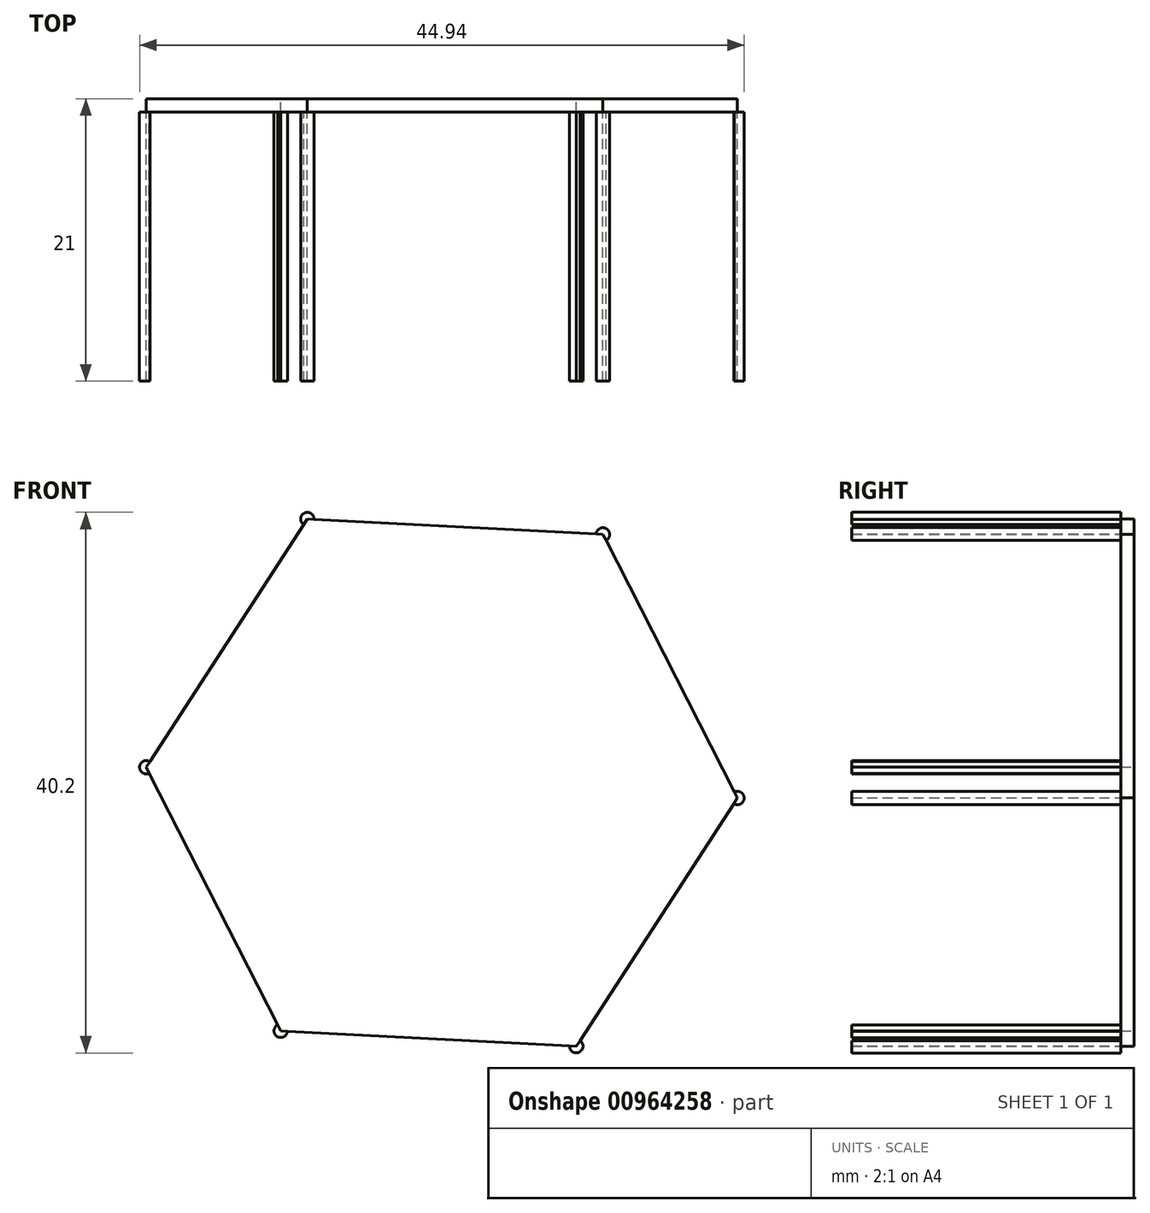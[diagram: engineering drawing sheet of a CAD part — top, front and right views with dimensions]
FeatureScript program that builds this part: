
annotation { "Feature Type Name" : "Feature", "Feature Type Description" : "" }
export const myFeature = defineFeature(function(context is Context, id is Id, definition is map)
    precondition{}
    {
        {
            var Q0;
            Q0=qCreatedBy(makeId("Front.planeOp"),FACE);
            var sketch = newSketch(context, id + "F0", { "sketchPlane" : qUnion([Q0])});
            skCircle(sketch, "E0.cCircle", {"center": v(-53.24, 58.34) * mm, "radius": 19.05 * mm, "construction": true});
            skLineSegment(sketch, "E0.0", {"start": v(-31.27, 57.2) * mm, "end": v(-43.25, 38.74) * mm});
            skLineSegment(sketch, "E0.1", {"start": v(-43.25, 38.74) * mm, "end": v(-65.22, 39.89) * mm});
            skLineSegment(sketch, "E0.2", {"start": v(-65.22, 39.89) * mm, "end": v(-75.21, 59.48) * mm});
            skLineSegment(sketch, "E0.3", {"start": v(-75.21, 59.48) * mm, "end": v(-63.24, 77.94) * mm});
            skLineSegment(sketch, "E0.4", {"start": v(-63.24, 77.94) * mm, "end": v(-41.27, 76.8) * mm});
            skLineSegment(sketch, "E0.5", {"start": v(-41.27, 76.8) * mm, "end": v(-31.27, 57.2) * mm});
            skPoint(sketch, "E0.0.midPoint", {"position": v(-37.26, 47.97) * mm});
            skSolve(sketch);
        }
        {
            var Q0;
            Q0=makeQuery(id+"F0.imprint","IMPRINT",FACE,{"disambiguationData":[TD([[makeQuery(id+"F0.imprint","IMPRINT",EDGE,{"derivedFrom":sQuery(id+"F0.wireOp",EDGE,"E0.0")}),-1.0]])]});
            extrude(context, id + "F1", {"entities" : qUnion([Q0]), "depth" : 1 * mm, "offsetDistance" : 25 * mm});
        }
        {
            var Q0;
            Q0=makeQuery(id+"F1.opExtrude","CAP_FACE",FACE,{"disambiguationData":[OSD([sQuery(id+"F0.wireOp",EDGE,"E0.0"),sQuery(id+"F0.wireOp",EDGE,"E0.1"),sQuery(id+"F0.wireOp",EDGE,"E0.2"),sQuery(id+"F0.wireOp",EDGE,"E0.3"),sQuery(id+"F0.wireOp",EDGE,"E0.4"),sQuery(id+"F0.wireOp",EDGE,"E0.5")])],"isStart":false});
            var sketch = newSketch(context, id + "F2", { "sketchPlane" : qUnion([Q0])});
            skCircle(sketch, "E1", {"center": v(-63.24, 77.94) * mm, "radius": 0.5 * mm});
            skCircle(sketch, "E2", {"center": v(-75.21, 59.48) * mm, "radius": 0.5 * mm});
            skCircle(sketch, "E3", {"center": v(-65.22, 39.89) * mm, "radius": 0.5 * mm});
            skCircle(sketch, "E4", {"center": v(-41.27, 76.8) * mm, "radius": 0.5 * mm});
            skCircle(sketch, "E5", {"center": v(-31.27, 57.2) * mm, "radius": 0.5 * mm});
            skCircle(sketch, "E6", {"center": v(-43.25, 38.74) * mm, "radius": 0.5 * mm});
            skSolve(sketch);
        }
        {
            var Q0;
            {var subQ0=sQuery(id+"F2.wireOp",EDGE,"E1");var subQ1=makeQuery(id+"F1.opExtrude","CAP_EDGE",EDGE,{"disambiguationData":[OSD([sQuery(id+"F0.wireOp",EDGE,"E0.3")])],"isStart":false});var subQ2=makeQuery(id+"F2.imprint","INTERSECT",VERTEX,{"derivedFrom":[subQ1,subQ0]});Q0=makeQuery(id+"F2.imprint","IMPRINT",FACE,{"disambiguationData":[TD([[makeQuery(id+"F2.imprint","IMPRINT",EDGE,{"disambiguationData":[TD([[subQ2,1.0]])],"derivedFrom":subQ0}),1.0]])]});}
            var Q1;
            {var subQ0=sQuery(id+"F2.wireOp",EDGE,"E4");var subQ1=makeQuery(id+"F1.opExtrude","CAP_EDGE",EDGE,{"disambiguationData":[OSD([sQuery(id+"F0.wireOp",EDGE,"E0.4")])],"isStart":false});var subQ2=makeQuery(id+"F2.imprint","INTERSECT",VERTEX,{"derivedFrom":[subQ1,subQ0]});Q1=makeQuery(id+"F2.imprint","IMPRINT",FACE,{"disambiguationData":[TD([[makeQuery(id+"F2.imprint","IMPRINT",EDGE,{"disambiguationData":[TD([[subQ2,1.0]])],"derivedFrom":subQ0}),1.0]])]});}
            var Q2;
            {var subQ0=sQuery(id+"F2.wireOp",EDGE,"E5");var subQ1=makeQuery(id+"F1.opExtrude","CAP_EDGE",EDGE,{"disambiguationData":[OSD([sQuery(id+"F0.wireOp",EDGE,"E0.0")])],"isStart":false});var subQ2=makeQuery(id+"F2.imprint","INTERSECT",VERTEX,{"derivedFrom":[subQ1,subQ0]});Q2=makeQuery(id+"F2.imprint","IMPRINT",FACE,{"disambiguationData":[TD([[makeQuery(id+"F2.imprint","IMPRINT",EDGE,{"disambiguationData":[TD([[subQ2,-1.0]])],"derivedFrom":subQ0}),1.0]])]});}
            var Q3;
            {var subQ0=sQuery(id+"F2.wireOp",EDGE,"E6");var subQ1=makeQuery(id+"F1.opExtrude","CAP_EDGE",EDGE,{"disambiguationData":[OSD([sQuery(id+"F0.wireOp",EDGE,"E0.0")])],"isStart":false});var subQ2=makeQuery(id+"F2.imprint","INTERSECT",VERTEX,{"derivedFrom":[subQ1,subQ0]});Q3=makeQuery(id+"F2.imprint","IMPRINT",FACE,{"disambiguationData":[TD([[makeQuery(id+"F2.imprint","IMPRINT",EDGE,{"disambiguationData":[TD([[subQ2,1.0]])],"derivedFrom":subQ0}),1.0]])]});}
            var Q4;
            {var subQ0=sQuery(id+"F2.wireOp",EDGE,"E3");var subQ1=makeQuery(id+"F1.opExtrude","CAP_EDGE",EDGE,{"disambiguationData":[OSD([sQuery(id+"F0.wireOp",EDGE,"E0.1")])],"isStart":false});var subQ2=makeQuery(id+"F2.imprint","INTERSECT",VERTEX,{"derivedFrom":[subQ1,subQ0]});Q4=makeQuery(id+"F2.imprint","IMPRINT",FACE,{"disambiguationData":[TD([[makeQuery(id+"F2.imprint","IMPRINT",EDGE,{"disambiguationData":[TD([[subQ2,1.0]])],"derivedFrom":subQ0}),1.0]])]});}
            var Q5;
            {var subQ0=sQuery(id+"F2.wireOp",EDGE,"E2");var subQ1=makeQuery(id+"F1.opExtrude","CAP_EDGE",EDGE,{"disambiguationData":[OSD([sQuery(id+"F0.wireOp",EDGE,"E0.2")])],"isStart":false});var subQ2=makeQuery(id+"F2.imprint","INTERSECT",VERTEX,{"derivedFrom":[subQ1,subQ0]});Q5=makeQuery(id+"F2.imprint","IMPRINT",FACE,{"disambiguationData":[TD([[makeQuery(id+"F2.imprint","IMPRINT",EDGE,{"disambiguationData":[TD([[subQ2,1.0]])],"derivedFrom":subQ0}),1.0]])]});}
            extrude(context, id + "F3", {"entities" : qUnion([Q0, Q1, Q2, Q3, Q4, Q5]), "depth" : 20 * mm, "offsetDistance" : 25 * mm});
        }
    });
